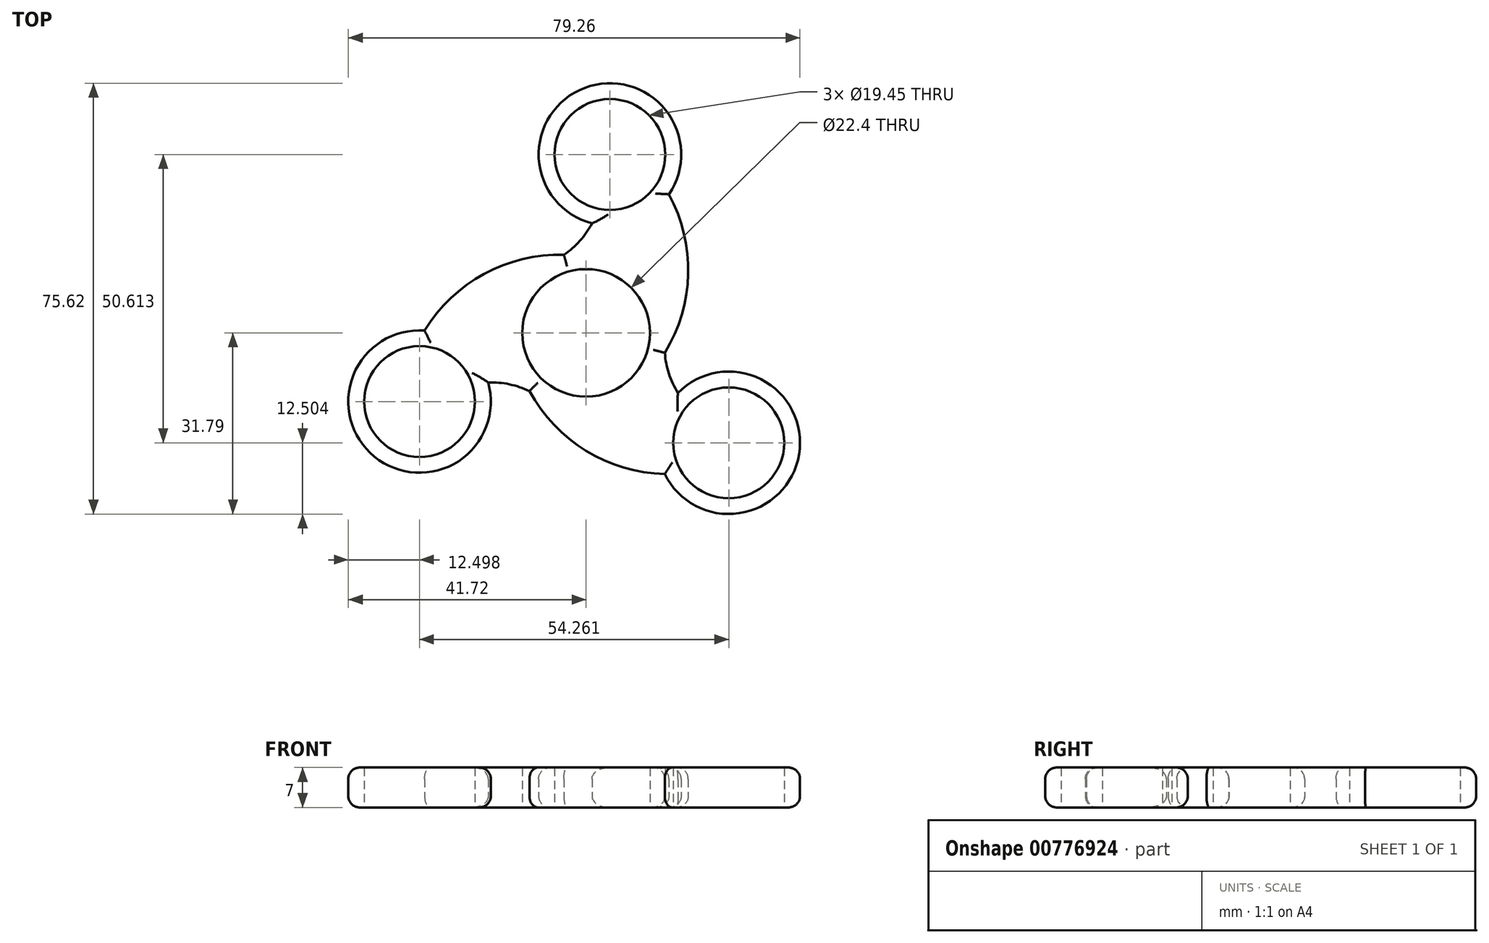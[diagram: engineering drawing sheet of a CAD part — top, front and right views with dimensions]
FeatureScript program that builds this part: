
annotation { "Feature Type Name" : "Feature", "Feature Type Description" : "" }
export const myFeature = defineFeature(function(context is Context, id is Id, definition is map)
    precondition{}
    {
        {
            var Q0;
            Q0=qCreatedBy(makeId("Top.planeOp"),FACE);
            var sketch = newSketch(context, id + "F0", { "sketchPlane" : qUnion([Q0])});
            skCircle(sketch, "E0", {"center": v(0, 0) * mm, "radius": 11.2 * mm});
            skArc(sketch, "E1", {"start": v(-9.94, -10.23) * mm, "mid": v(-0.01, -20.67) * mm, "end": v(13.8, -24.76) * mm});
            skArc(sketch, "E2", {"start": v(13.83, -3.5) * mm, "mid": v(14.54, -7.15) * mm, "end": v(16.13, -10.52) * mm});
            skCircle(sketch, "E3", {"center": v(25.04, -19.29) * mm, "radius": 9.72 * mm});
            skArc(sketch, "E4", {"start": v(13.8, -24.76) * mm, "mid": v(37.38, -21.3) * mm, "end": v(16.13, -10.52) * mm});
            skArc(sketch, "E5.1.0", {"start": v(-3.9, 13.72) * mm, "mid": v(-1.08, 16.16) * mm, "end": v(1.05, 19.23) * mm});
            skCircle(sketch, "E5.1.1", {"center": v(4.18, 31.33) * mm, "radius": 9.72 * mm});
            skArc(sketch, "E5.1.2", {"start": v(14.54, 24.34) * mm, "mid": v(-0.24, 43.02) * mm, "end": v(1.05, 19.23) * mm});
            skArc(sketch, "E5.1.3", {"start": v(13.83, -3.5) * mm, "mid": v(17.91, 10.33) * mm, "end": v(14.54, 24.34) * mm});
            skArc(sketch, "E5.2.0", {"start": v(-9.94, -10.23) * mm, "mid": v(-13.46, -9.01) * mm, "end": v(-17.17, -8.7) * mm});
            skCircle(sketch, "E5.2.1", {"center": v(-29.22, -12.04) * mm, "radius": 9.72 * mm});
            skArc(sketch, "E5.2.2", {"start": v(-28.35, 0.43) * mm, "mid": v(-37.13, -21.72) * mm, "end": v(-17.17, -8.7) * mm});
            skArc(sketch, "E5.2.3", {"start": v(-3.9, 13.72) * mm, "mid": v(-17.9, 10.35) * mm, "end": v(-28.35, 0.43) * mm});
            skPoint(sketch, "E6.trimOffspring.end.orphan", {"position": v(14, 0) * mm});
            skPoint(sketch, "E7.orphan", {"position": v(13.34, -4.26) * mm});
            skPoint(sketch, "E8.orphan", {"position": v(-7, -12.12) * mm});
            skPoint(sketch, "E9.orphan", {"position": v(-10.36, -9.42) * mm});
            skPoint(sketch, "E10.orphan", {"position": v(-7, 12.12) * mm});
            skPoint(sketch, "E11.orphan", {"position": v(-2.98, 13.68) * mm});
            skSolve(sketch);
        }
        {
            var Q0;
            Q0=qSketchRegion(id+"F0",true);
            extrude(context, id + "F1", {"entities" : qUnion([Q0]), "depth" : 7 * mm, "offsetDistance" : 25 * mm});
        }
        {
            var Q0;
            Q0=makeQuery(id+"F1.opExtrude","CAP_EDGE",EDGE,{"disambiguationData":[OSD([sQuery(id+"F0.wireOp",EDGE,"E5.2.2")])],"isStart":false});
            var Q1;
            Q1=makeQuery(id+"F1.opExtrude","CAP_EDGE",EDGE,{"disambiguationData":[OSD([sQuery(id+"F0.wireOp",EDGE,"E5.2.2")])],"isStart":true});
            var Q2;
            Q2=makeQuery(id+"F1.opExtrude","CAP_EDGE",EDGE,{"disambiguationData":[OSD([sQuery(id+"F0.wireOp",EDGE,"E5.2.0")])],"isStart":true});
            var Q3;
            Q3=makeQuery(id+"F1.opExtrude","CAP_EDGE",EDGE,{"disambiguationData":[OSD([sQuery(id+"F0.wireOp",EDGE,"E5.2.0")])],"isStart":false});
            var Q4;
            Q4=makeQuery(id+"F1.opExtrude","CAP_EDGE",EDGE,{"disambiguationData":[OSD([sQuery(id+"F0.wireOp",EDGE,"E1")])],"isStart":false});
            var Q5;
            Q5=makeQuery(id+"F1.opExtrude","CAP_EDGE",EDGE,{"disambiguationData":[OSD([sQuery(id+"F0.wireOp",EDGE,"E4")])],"isStart":true});
            var Q6;
            Q6=makeQuery(id+"F1.opExtrude","CAP_EDGE",EDGE,{"disambiguationData":[OSD([sQuery(id+"F0.wireOp",EDGE,"E4")])],"isStart":false});
            var Q7;
            Q7=makeQuery(id+"F1.opExtrude","CAP_EDGE",EDGE,{"disambiguationData":[OSD([sQuery(id+"F0.wireOp",EDGE,"E2")])],"isStart":false});
            var Q8;
            Q8=makeQuery(id+"F1.opExtrude","CAP_EDGE",EDGE,{"disambiguationData":[OSD([sQuery(id+"F0.wireOp",EDGE,"E5.1.3")])],"isStart":false});
            var Q9;
            Q9=makeQuery(id+"F1.opExtrude","CAP_EDGE",EDGE,{"disambiguationData":[OSD([sQuery(id+"F0.wireOp",EDGE,"E5.1.3")])],"isStart":true});
            var Q10;
            Q10=makeQuery(id+"F1.opExtrude","CAP_EDGE",EDGE,{"disambiguationData":[OSD([sQuery(id+"F0.wireOp",EDGE,"E1")])],"isStart":true});
            var Q11;
            Q11=makeQuery(id+"F1.opExtrude","CAP_EDGE",EDGE,{"disambiguationData":[OSD([sQuery(id+"F0.wireOp",EDGE,"E2")])],"isStart":true});
            var Q12;
            Q12=makeQuery(id+"F1.opExtrude","CAP_EDGE",EDGE,{"disambiguationData":[OSD([sQuery(id+"F0.wireOp",EDGE,"E5.1.2")])],"isStart":true});
            var Q13;
            Q13=makeQuery(id+"F1.opExtrude","CAP_EDGE",EDGE,{"disambiguationData":[OSD([sQuery(id+"F0.wireOp",EDGE,"E5.1.2")])],"isStart":false});
            var Q14;
            Q14=makeQuery(id+"F1.opExtrude","CAP_EDGE",EDGE,{"disambiguationData":[OSD([sQuery(id+"F0.wireOp",EDGE,"E5.2.3")])],"isStart":true});
            var Q15;
            Q15=makeQuery(id+"F1.opExtrude","CAP_EDGE",EDGE,{"disambiguationData":[OSD([sQuery(id+"F0.wireOp",EDGE,"E5.2.3")])],"isStart":false});
            var Q16;
            Q16=makeQuery(id+"F1.opExtrude","CAP_EDGE",EDGE,{"disambiguationData":[OSD([sQuery(id+"F0.wireOp",EDGE,"E5.1.0")])],"isStart":false});
            var Q17;
            Q17=makeQuery(id+"F1.opExtrude","CAP_EDGE",EDGE,{"disambiguationData":[OSD([sQuery(id+"F0.wireOp",EDGE,"E5.1.0")])],"isStart":true});
            fillet(context, id + "F2", {"entities" : qUnion([Q0, Q1, Q2, Q3, Q4, Q5, Q6, Q7, Q8, Q9, Q10, Q11, Q12, Q13, Q14, Q15, Q16, Q17]), "radius" : 2 * mm, "tangentPropagation" : true, "allowEdgeOverflow" : false});
        }
    });
